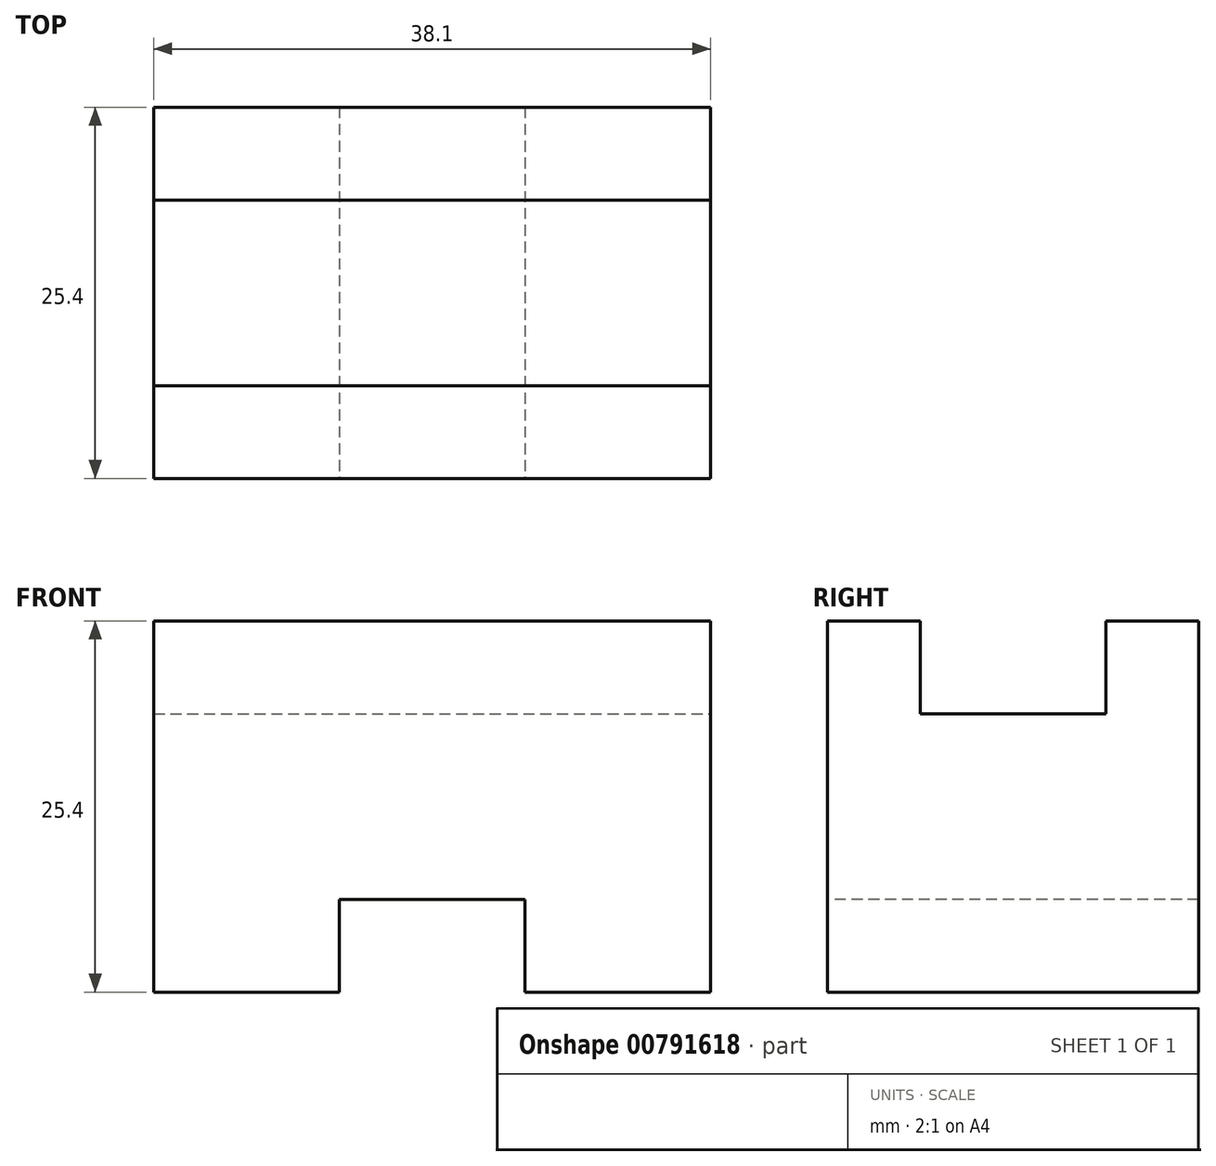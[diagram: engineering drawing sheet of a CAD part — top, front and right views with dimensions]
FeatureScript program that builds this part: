
annotation { "Feature Type Name" : "Feature", "Feature Type Description" : "" }
export const myFeature = defineFeature(function(context is Context, id is Id, definition is map)
    precondition{}
    {
        {
            var Q0;
            Q0=qCreatedBy(makeId("Front.planeOp"),FACE);
            var sketch = newSketch(context, id + "F0", { "sketchPlane" : qUnion([Q0])});
            skLineSegment(sketch, "E0", {"start": v(0, 0) * mm, "end": v(38.1, 0) * mm});
            skLineSegment(sketch, "E1", {"start": v(38.1, 0) * mm, "end": v(38.1, 25.4) * mm});
            skLineSegment(sketch, "E2", {"start": v(38.1, 25.4) * mm, "end": v(0, 25.4) * mm});
            skLineSegment(sketch, "E3", {"start": v(0, 25.4) * mm, "end": v(0, 0) * mm});
            skSolve(sketch);
        }
        {
            var Q0;
            Q0 = qSketchRegion(id + "F0", true);
            extrude(context, id + "F1", {"entities" : qUnion([Q0]), "depth" : 25.4 * mm, "offsetDistance" : 25.4 * mm});
        }
        {
            var Q0;
            Q0=makeQuery(id+"F1.opExtrude","CAP_FACE",FACE,{"disambiguationData":[OSD([sQuery(id+"F0.wireOp",EDGE,"E0"),sQuery(id+"F0.wireOp",EDGE,"E1"),sQuery(id+"F0.wireOp",EDGE,"E2"),sQuery(id+"F0.wireOp",EDGE,"E3")])],"isStart":false});
            var sketch = newSketch(context, id + "F2", { "sketchPlane" : qUnion([Q0])});
            skLineSegment(sketch, "E4", {"start": v(0, 0) * mm, "end": v(12.7, 0) * mm});
            skLineSegment(sketch, "E5", {"start": v(12.7, 0) * mm, "end": v(12.7, 6.35) * mm});
            skLineSegment(sketch, "E6", {"start": v(12.7, 6.35) * mm, "end": v(25.4, 6.35) * mm});
            skLineSegment(sketch, "E7", {"start": v(25.4, 6.35) * mm, "end": v(25.4, 0) * mm});
            skLineSegment(sketch, "E8", {"start": v(25.4, 0) * mm, "end": v(38.1, 0) * mm});
            skSolve(sketch);
        }
        {
            var Q0;
            Q0 = qSketchRegion(id + "F2", true);
            var Q1;
            {var subQ0=sQuery(id+"F2.wireOp",EDGE,"E5");Q1=makeQuery(id+"F2.imprint","IMPRINT",FACE,{"disambiguationData":[TD([[makeQuery(id+"F2.imprint","IMPRINT",EDGE,{"derivedFrom":subQ0}),-1.0]])]});}
            extrude(context, id + "F3", {"entities" : qUnion([Q0, Q1]), "operationType" : NewBodyOperationType.REMOVE, "oppositeDirection" : true, "depth" : 25.4 * mm, "offsetDistance" : 25.4 * mm});
        }
        {
            var Q0;
            Q0=makeQuery(id+"F1.opExtrude","SWEPT_FACE",FACE,{"disambiguationData":[OSD([sQuery(id+"F0.wireOp",EDGE,"E1")])]});
            var sketch = newSketch(context, id + "F4", { "sketchPlane" : qUnion([Q0])});
            skLineSegment(sketch, "E9", {"start": v(-25.4, 25.4) * mm, "end": v(-19.05, 25.4) * mm});
            skLineSegment(sketch, "E10", {"start": v(-19.05, 25.4) * mm, "end": v(-19.05, 19.05) * mm});
            skLineSegment(sketch, "E11", {"start": v(-19.05, 19.05) * mm, "end": v(-6.35, 19.05) * mm});
            skLineSegment(sketch, "E12", {"start": v(-6.35, 19.05) * mm, "end": v(-6.35, 25.4) * mm});
            skLineSegment(sketch, "E13", {"start": v(-6.35, 25.4) * mm, "end": v(0, 25.4) * mm});
            skSolve(sketch);
        }
        {
            var Q0;
            Q0 = qSketchRegion(id + "F4", true);
            var Q1;
            {var subQ0=sQuery(id+"F4.wireOp",EDGE,"E10");Q1=makeQuery(id+"F4.imprint","IMPRINT",FACE,{"disambiguationData":[TD([[makeQuery(id+"F4.imprint","IMPRINT",EDGE,{"derivedFrom":subQ0}),1.0]])]});}
            extrude(context, id + "F5", {"entities" : qUnion([Q0, Q1]), "operationType" : NewBodyOperationType.REMOVE, "endBound" : BoundingType.THROUGH_ALL, "oppositeDirection" : true, "depth" : 25.4 * mm, "offsetDistance" : 25.4 * mm});
        }
    });
